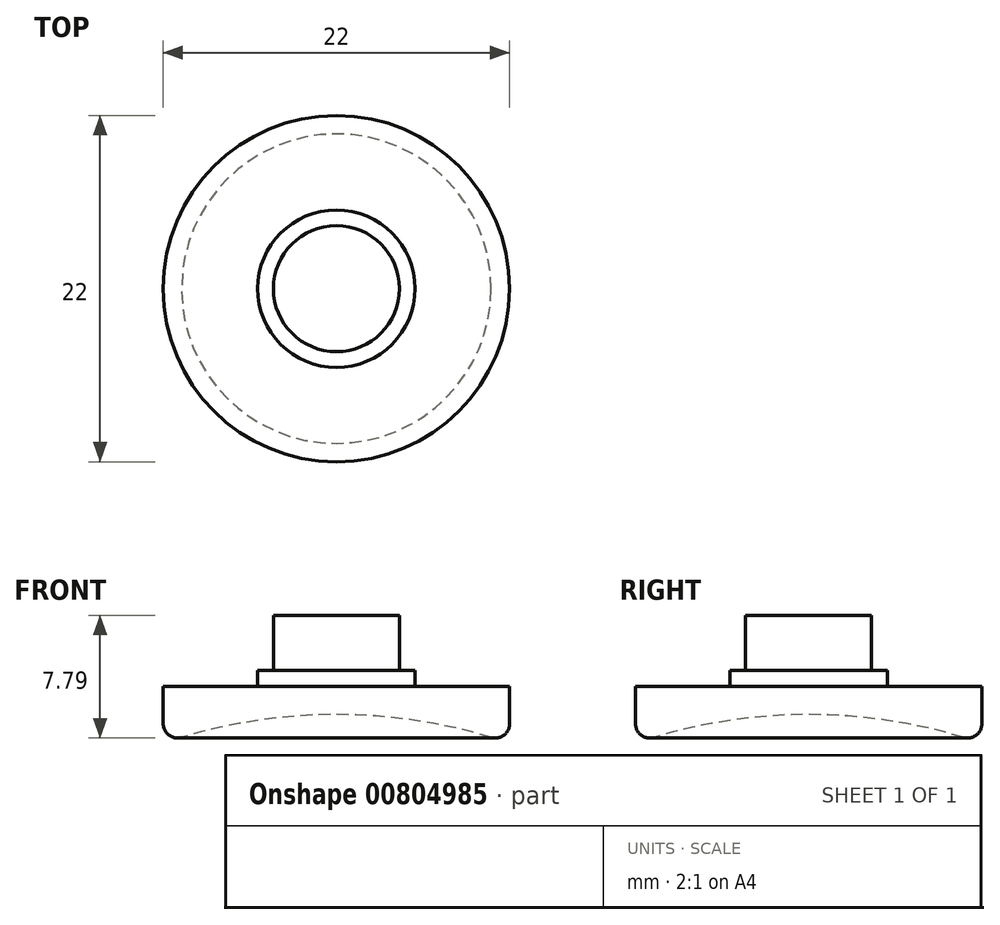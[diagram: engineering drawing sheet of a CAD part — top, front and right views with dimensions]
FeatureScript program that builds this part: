
annotation { "Feature Type Name" : "Feature", "Feature Type Description" : "" }
export const myFeature = defineFeature(function(context is Context, id is Id, definition is map)
    precondition{}
    {
        {
            var Q0;
            Q0=qCreatedBy(makeId("Top.planeOp"),FACE);
            var sketch = newSketch(context, id + "F0", { "sketchPlane" : qUnion([Q0])});
            skCircle(sketch, "E0", {"center": v(59.41, 64.06) * mm, "radius": 11 * mm});
            skSolve(sketch);
        }
        {
            var Q0;
            Q0=makeQuery(id+"F0.imprint","IMPRINT",FACE,{"disambiguationData":[TD([[makeQuery(id+"F0.imprint","IMPRINT",EDGE,{"derivedFrom":sQuery(id+"F0.wireOp",EDGE,"E0")}),1.0]])]});
            var Q1;
            Q1=makeQuery(id+"F0.imprint","IMPRINT",FACE,{"disambiguationData":[TD([[makeQuery(id+"F0.imprint","IMPRINT",EDGE,{"derivedFrom":sQuery(id+"F0.wireOp",EDGE,"2bYrixF8-2V4G-PsJT-iCTY-IxQZrD0WGVvQ")}),1.0]])]});
            extrude(context, id + "F1", {"entities" : qUnion([Q0, Q1]), "depth" : 3.5 * mm, "offsetDistance" : 25 * mm});
        }
        {
            var Q0;
            Q0=makeQuery(id+"F1.opExtrude","CAP_FACE",FACE,{"disambiguationData":[OSD([sQuery(id+"F0.wireOp",EDGE,"E0")])],"isStart":false});
            var sketch = newSketch(context, id + "F2", { "sketchPlane" : qUnion([Q0])});
            skPoint(sketch, "E1", {"position": v(59.41, 64.06) * mm});
            skCircle(sketch, "E2", {"center": v(59.41, 64.06) * mm, "radius": 5 * mm});
            skSolve(sketch);
        }
        {
            var Q0;
            Q0=qSketchRegion(id+"F2",true);
            extrude(context, id + "F3", {"entities" : qUnion([Q0]), "operationType" : NewBodyOperationType.ADD, "depth" : 1 * mm, "offsetDistance" : 25 * mm});
        }
        {
            var Q0;
            Q0=makeQuery(id+"F3.opExtrude","CAP_FACE",FACE,{"disambiguationData":[OSD([sQuery(id+"F2.wireOp",EDGE,"E2")])],"isStart":false});
            var sketch = newSketch(context, id + "F4", { "sketchPlane" : qUnion([Q0])});
            skPoint(sketch, "E3", {"position": v(59.41, 64.06) * mm});
            skCircle(sketch, "E4", {"center": v(59.41, 64.06) * mm, "radius": 4 * mm});
            skSolve(sketch);
        }
        {
            var Q0;
            Q0=makeQuery(id+"F4.imprint","IMPRINT",FACE,{"disambiguationData":[TD([[makeQuery(id+"F4.imprint","IMPRINT",EDGE,{"derivedFrom":sQuery(id+"F4.wireOp",EDGE,"E4")}),1.0]])]});
            extrude(context, id + "F5", {"entities" : qUnion([Q0]), "operationType" : NewBodyOperationType.ADD, "depth" : 3.5 * mm, "offsetDistance" : 25 * mm});
        }
        {
            var Q0;
            Q0=makeQuery(id+"F1.opExtrude","CAP_FACE",FACE,{"disambiguationData":[OSD([sQuery(id+"F0.wireOp",EDGE,"E0")])],"isStart":true});
            var sketch = newSketch(context, id + "F6", { "sketchPlane" : qUnion([Q0])});
            skCircle(sketch, "E5", {"center": v(59.41, -64.06) * mm, "radius": 1.35 * mm});
            skSolve(sketch);
        }
        {
            var Q0;
            Q0=makeQuery(id+"F6.imprint","IMPRINT",FACE,{"disambiguationData":[TD([[makeQuery(id+"F6.imprint","IMPRINT",EDGE,{"derivedFrom":sQuery(id+"F6.wireOp",EDGE,"E5")}),1.0]])]});
            extrude(context, id + "F7", {"entities" : qUnion([Q0]), "operationType" : NewBodyOperationType.ADD, "depth" : 32.3 * mm, "offsetDistance" : 25 * mm});
        }
        {
            var Q0;
            Q0=makeQuery(id+"F7.opExtrude","CAP_FACE",FACE,{"disambiguationData":[OSD([sQuery(id+"F6.wireOp",EDGE,"E5")])],"isStart":false});
            var sketch = newSketch(context, id + "F8", { "sketchPlane" : qUnion([Q0])});
            skCircle(sketch, "E6", {"center": v(59.41, -64.06) * mm, "radius": 34 * mm});
            skLineSegment(sketch, "E7", {"start": v(59.41, -64.06) * mm, "end": v(93.41, -64.06) * mm});
            skLineSegment(sketch, "E8", {"start": v(59.41, -64.06) * mm, "end": v(25.41, -64.06) * mm});
            skSolve(sketch);
        }
        {
            var Q0;
            {var subQ0=sQuery(id+"F8.wireOp",EDGE,"E7");var subQ1=sQuery(id+"F8.wireOp",EDGE,"E6");var subQ2=makeQuery(id+"F8.imprint","INTERSECT",VERTEX,{"derivedFrom":[subQ1,subQ0]});Q0=makeQuery(id+"F8.imprint","IMPRINT",FACE,{"disambiguationData":[TD([[makeQuery(id+"F8.imprint","IMPRINT",EDGE,{"disambiguationData":[TD([[subQ2,-1.0]])],"derivedFrom":subQ1}),1.0]])]});}
            var Q1;
            {var subQ0=sQuery(id+"F8.wireOp",EDGE,"E8");var subQ1=sQuery(id+"F8.wireOp",EDGE,"E7");var subQ2=makeQuery(id+"F8.imprint","INTERSECT",VERTEX,{"derivedFrom":[subQ1,subQ0]});Q1=makeQuery(id+"F8.imprint","IMPRINT",FACE,{"disambiguationData":[TD([[makeQuery(id+"F8.imprint","IMPRINT",EDGE,{"disambiguationData":[TD([[subQ2,-1.0]])],"derivedFrom":subQ1}),1.0]])]});}
            var Q2;
            Q2=sQuery(id+"F8.wireOp",EDGE,"E7");
            revolve(context, id + "F9", {"operationType" : NewBodyOperationType.REMOVE, "surfaceOperationType" : NewSurfaceOperationType.NEW, "entities" : qUnion([Q0, Q1]), "axis" : qUnion([Q2]), "revolveType" : RevolveType.FULL});
        }
        {
            var Q0;
            Q0=makeQuery(id+"F9.boolean.opBoolean","INTERSECT",EDGE,{"derivedFrom":[makeQuery(id+"F1.opExtrude","CAP_FACE",FACE,{"disambiguationData":[OSD([sQuery(id+"F0.wireOp",EDGE,"E0")])],"isStart":true}),makeQuery(id+"F9.opRevolve","SWEPT_FACE",FACE,{"disambiguationData":[OSD([sQuery(id+"F8.wireOp",EDGE,"E6")])]})]});
            fillet(context, id + "F10", {"entities" : qUnion([Q0]), "radius" : 5 * mm, "tangentPropagation" : true, "allowEdgeOverflow" : false});
        }
        {
            var Q0;
            {var subQ0=sQuery(id+"F0.wireOp",EDGE,"E0");Q0=makeQuery(id+"F10.opFillet","BLEND_EDGE",EDGE,{"blendedFrom":[makeQuery(id+"F9.boolean.opBoolean","INTERSECT",EDGE,{"derivedFrom":[makeQuery(id+"F1.opExtrude","CAP_FACE",FACE,{"disambiguationData":[OSD([subQ0])],"isStart":true}),makeQuery(id+"F9.opRevolve","SWEPT_FACE",FACE,{"disambiguationData":[OSD([sQuery(id+"F8.wireOp",EDGE,"E6")])]})]}),makeQuery(id+"F1.opExtrude","SWEPT_FACE",FACE,{"disambiguationData":[OSD([subQ0])]})],"blendedInto":[makeQuery(id+"F1.opExtrude","SWEPT_FACE",FACE,{"disambiguationData":[OSD([subQ0])]})]});}
            fillet(context, id + "F11", {"entities" : qUnion([Q0]), "radius" : 0.9 * mm, "tangentPropagation" : true, "allowEdgeOverflow" : false});
        }
    });
